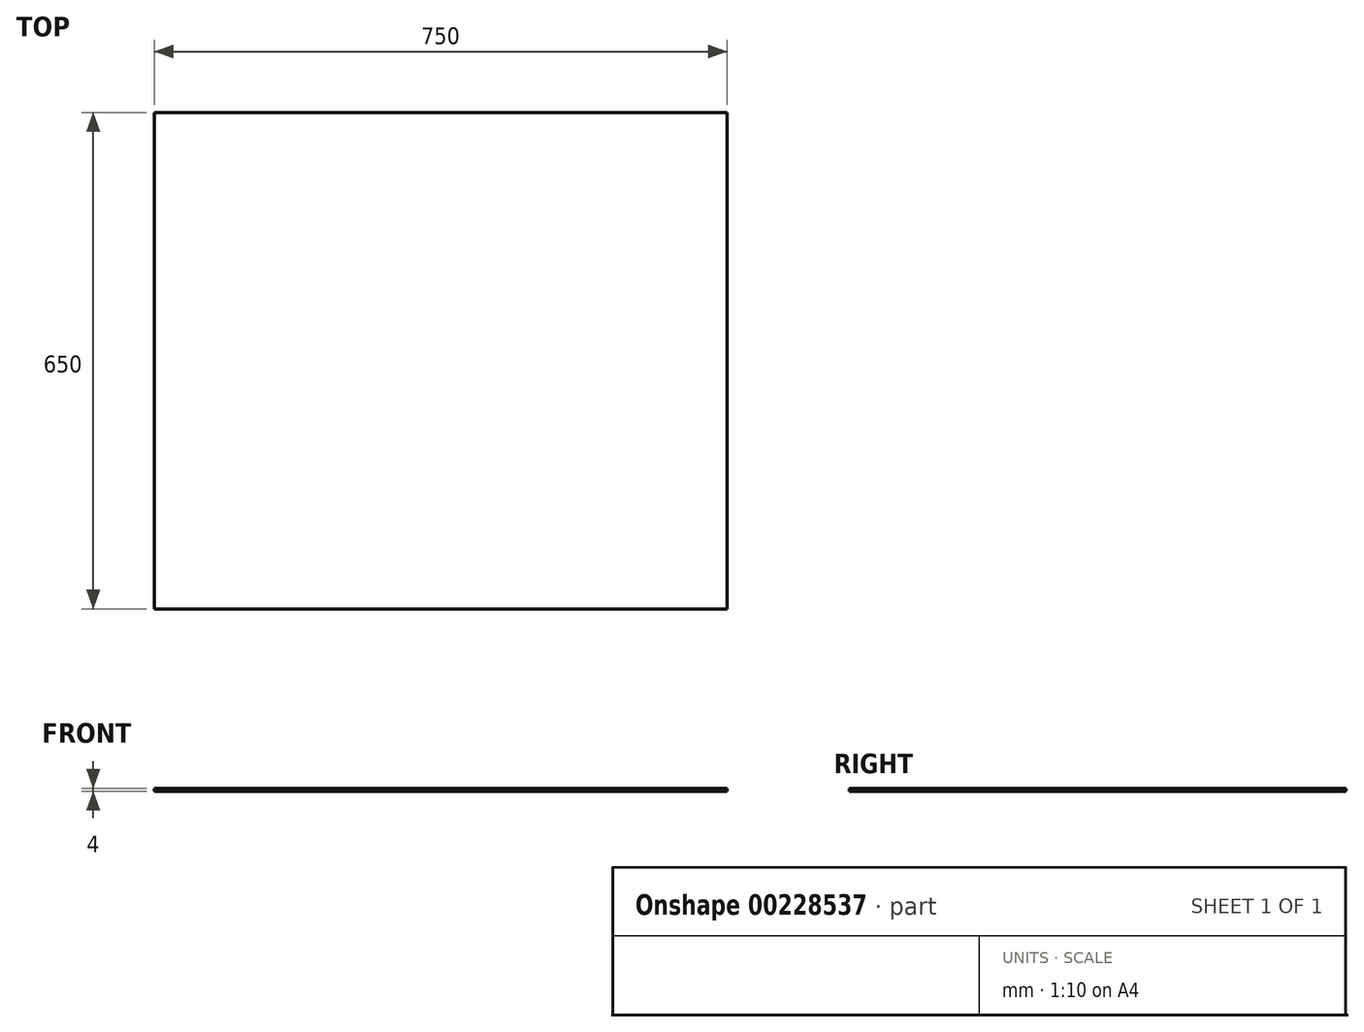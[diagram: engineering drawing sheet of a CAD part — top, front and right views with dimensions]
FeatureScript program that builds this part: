
annotation { "Feature Type Name" : "Feature", "Feature Type Description" : "" }
export const myFeature = defineFeature(function(context is Context, id is Id, definition is map)
    precondition{}
    {
        {
            var Q0;
            Q0=qCreatedBy(makeId("Top.planeOp"),FACE);
            var sketch = newSketch(context, id + "F0", { "sketchPlane" : qUnion([Q0])});
            skLineSegment(sketch, "E0.bottom", {"start": v(375, 325) * mm, "end": v(-375, 325) * mm});
            skLineSegment(sketch, "E0.top", {"start": v(375, -325) * mm, "end": v(-375, -325) * mm});
            skLineSegment(sketch, "E0.left", {"start": v(375, 325) * mm, "end": v(375, -325) * mm});
            skLineSegment(sketch, "E0.right", {"start": v(-375, 325) * mm, "end": v(-375, -325) * mm});
            skPoint(sketch, "E0.middle", {"position": v(0, 0) * mm});
            skSolve(sketch);
        }
        {
            var Q0;
            Q0=makeQuery(id+"F0.imprint","IMPRINT",FACE,{"disambiguationData":[TD([[makeQuery(id+"F0.imprint","IMPRINT",EDGE,{"derivedFrom":sQuery(id+"F0.wireOp",EDGE,"E0.bottom")}),1.0]])]});
            extrude(context, id + "F1", {"entities" : qUnion([Q0]), "oppositeDirection" : true, "depth" : 4 * mm});
        }
    });
